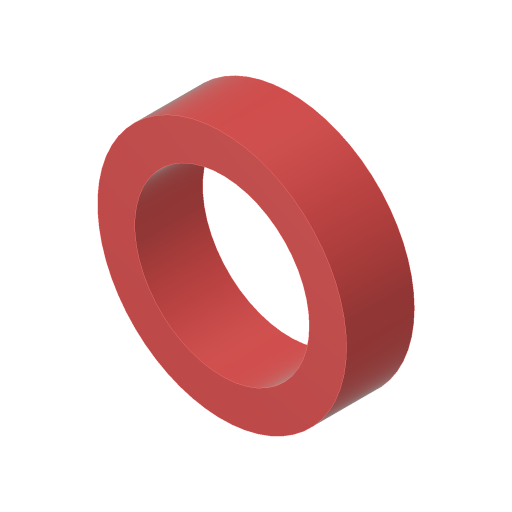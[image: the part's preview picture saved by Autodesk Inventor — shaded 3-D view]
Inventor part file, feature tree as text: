
AUTODESK INVENTOR PART (.ipt)
format: ipt  version: 2023.4 (Build 274418000, 418)  size: 111,616 bytes
history: native  units: in
note: dims shown in document units (in); Inventor stores cm internally (conversion verified against a paired STEP export)
features: extrude x1, sketch x1
ambient origin geometry x8: Origin, YZ Plane, XZ Plane, XY Plane, X Axis, Y Axis, Z Axis, Center Point
bodies: Solid1 (feature_tree)
feature tree (2):
  extrude  "Extrusion1"  Depth=0.2275in
  sketch  "Sketch1"  dims[d0=0.585in d1=0.125in d2=0.2275in d3=0.0in]
